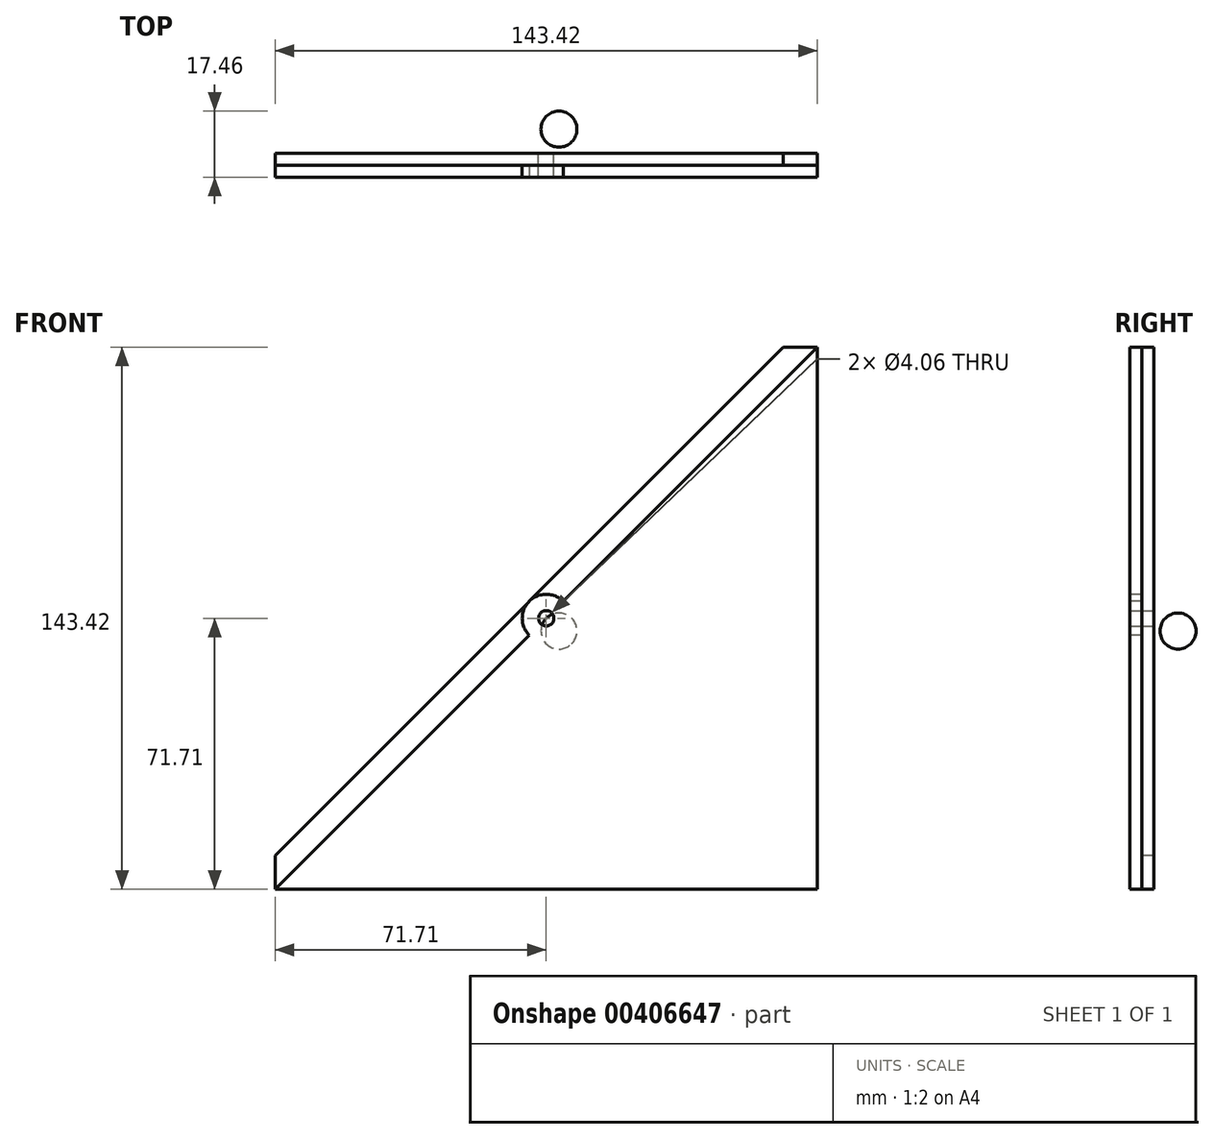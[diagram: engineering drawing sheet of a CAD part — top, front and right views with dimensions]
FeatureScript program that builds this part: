
annotation { "Feature Type Name" : "Feature", "Feature Type Description" : "" }
export const myFeature = defineFeature(function(context is Context, id is Id, definition is map)
    precondition{}
    {
        {
            var Q0;
            Q0=qCreatedBy(makeId("Front.planeOp"),FACE);
            var sketch = newSketch(context, id + "F0", { "sketchPlane" : qUnion([Q0])});
            skLineSegment(sketch, "E0.bottom", {"start": v(-76.2, 76.2) * mm, "end": v(76.2, 76.2) * mm, "construction": true});
            skLineSegment(sketch, "E0.top", {"start": v(-76.2, -76.2) * mm, "end": v(76.2, -76.2) * mm});
            skLineSegment(sketch, "E0.left", {"start": v(-76.2, 76.2) * mm, "end": v(-76.2, -76.2) * mm, "construction": true});
            skLineSegment(sketch, "E0.right", {"start": v(76.2, 76.2) * mm, "end": v(76.2, -76.2) * mm});
            skPoint(sketch, "E0.middle", {"position": v(0, 0) * mm});
            skLineSegment(sketch, "E1", {"start": v(-76.2, -76.2) * mm, "end": v(76.2, 76.2) * mm});
            skLineSegment(sketch, "E2", {"start": v(-76.2, 76.2) * mm, "end": v(76.2, -76.2) * mm, "construction": true});
            skCircle(sketch, "E3", {"center": v(4.5, -4.5) * mm, "radius": 6.35 * mm, "construction": true});
            skCircle(sketch, "E4", {"center": v(4.5, -4.5) * mm, "radius": 2.03 * mm});
            skSolve(sketch);
        }
        {
            var Q0;
            Q0=qSketchRegion(id+"F0",true);
            var Q1;
            Q1=sQuery(id+"F0.wireOp",EDGE,"E0.bottom");
            var Q2;
            Q2=sQuery(id+"F0.wireOp",EDGE,"E0.left");
            extrude(context, id + "F1", {"entities" : qUnion([Q0]), "surfaceEntities" : qUnion([Q1, Q2]), "depth" : 3.17 * mm});
        }
        {
            var Q0;
            Q0=sQuery(id+"F0.wireOp",VERTEX,"E4.center");
            var Q1;
            Q1=qCreatedBy(makeId("Top.planeOp"),FACE);
            cPlane(context, id + "F2", {"entities" : qUnion([Q0, Q1]), "cplaneType" : CPlaneType.PLANE_POINT, "offset" : 25.4 * mm, "width" : 152.4 * mm, "height" : 152.4 * mm});
        }
        {
            var Q0;
            Q0=qCreatedBy(id+"F2.planeOp",FACE);
            var sketch = newSketch(context, id + "F3", { "sketchPlane" : qUnion([Q0])});
            skPoint(sketch, "E5.0", {"position": v(4.5, 0) * mm});
            skLineSegment(sketch, "E6", {"start": v(4.5, 0) * mm, "end": v(4.5, -119.12) * mm});
            skSolve(sketch);
        }
        {
            var Q0;
            Q0=makeQuery(id+"F1.opExtrude","SWEPT_BODY",BODY,{"disambiguationData":[OSD([sQuery(id+"F0.wireOp",EDGE,"E0.top"),sQuery(id+"F0.wireOp",EDGE,"E0.right"),sQuery(id+"F0.wireOp",EDGE,"E1"),sQuery(id+"F0.wireOp",EDGE,"E4")])]});
            var Q1;
            Q1=sQuery(id+"F3.wireOp",EDGE,"E6");
            var Q2;
            Q2=sQuery(id+"F3.wireOp",EDGE,"E6");
            transform(context, id + "F4", {"entities" : qUnion([Q0]), "transformType" : TransformType.ROTATION, "transformAxis" : qUnion([Q2]), "angle" : 90 * degree, "makeCopy" : true});
        }
        {
            var Q0;
            Q0=makeQuery(id+"F4.opPattern","COPY",BODY,{"derivedFrom":makeQuery(id+"F1.opExtrude","SWEPT_BODY",BODY,{"disambiguationData":[OSD([sQuery(id+"F0.wireOp",EDGE,"E0.top"),sQuery(id+"F0.wireOp",EDGE,"E0.right"),sQuery(id+"F0.wireOp",EDGE,"E1"),sQuery(id+"F0.wireOp",EDGE,"E4")])]}),"instanceName":"1"});
            var Q1;
            Q1=sQuery(id+"F3.wireOp",EDGE,"E6");
            transform(context, id + "F5", {"entities" : qUnion([Q0]), "transformType" : TransformType.TRANSLATION_DISTANCE, "transformDirection" : qUnion([Q1]), "distance" : 3.17 * mm, "makeCopy" : false});
        }
        {
            var Q0;
            Q0=makeQuery(id+"F4.opPattern","COPY",FACE,{"derivedFrom":makeQuery(id+"F1.opExtrude","CAP_FACE",FACE,{"disambiguationData":[OSD([sQuery(id+"F0.wireOp",EDGE,"E0.top"),sQuery(id+"F0.wireOp",EDGE,"E0.right"),sQuery(id+"F0.wireOp",EDGE,"E1"),sQuery(id+"F0.wireOp",EDGE,"E4")])],"isStart":false}),"instanceName":"1"});
            var sketch = newSketch(context, id + "F6", { "sketchPlane" : qUnion([Q0])});
            skCircle(sketch, "E7.1", {"center": v(4.5, -4.5) * mm, "radius": 6.35 * mm});
            skSolve(sketch);
        }
        {
            var Q0;
            Q0=qSketchRegion(id+"F6",true);
            extrude(context, id + "F7", {"entities" : qUnion([Q0]), "depth" : 6.35 * mm});
        }
        {
            var Q0;
            Q0=makeQuery(id+"F4.opPattern","COPY",FACE,{"derivedFrom":makeQuery(id+"F1.opExtrude","CAP_FACE",FACE,{"disambiguationData":[OSD([sQuery(id+"F0.wireOp",EDGE,"E0.top"),sQuery(id+"F0.wireOp",EDGE,"E0.right"),sQuery(id+"F0.wireOp",EDGE,"E1"),sQuery(id+"F0.wireOp",EDGE,"E4")])],"isStart":false}),"instanceName":"1"});
            var sketch = newSketch(context, id + "F8", { "sketchPlane" : qUnion([Q0])});
            skArc(sketch, "E8.0", {"start": v(0, 0) * mm, "mid": v(0, -8.98) * mm, "end": v(8.98, -8.98) * mm});
            skLineSegment(sketch, "E9.0", {"start": v(76.2, -85.18) * mm, "end": v(-76.2, 67.22) * mm});
            skLineSegment(sketch, "E10", {"start": v(0, 0) * mm, "end": v(-67.22, 67.22) * mm});
            skLineSegment(sketch, "E11", {"start": v(8.98, -8.98) * mm, "end": v(76.2, -76.2) * mm});
            skLineSegment(sketch, "E12", {"start": v(-76.2, 67.22) * mm, "end": v(-67.22, 67.22) * mm});
            skLineSegment(sketch, "E13", {"start": v(76.2, -85.18) * mm, "end": v(76.2, -76.2) * mm});
            skSolve(sketch);
        }
        {
            var Q0;
            Q0 = qSketchRegion(id + "F8", true);
            extrude(context, id + "F9", {"entities" : qUnion([Q0]), "operationType" : NewBodyOperationType.REMOVE, "endBound" : BoundingType.UP_TO_NEXT, "oppositeDirection" : true, "depth" : 25.4 * mm});
        }
        {
            var Q0;
            Q0=makeQuery(id+"F4.opPattern","COPY",FACE,{"derivedFrom":makeQuery(id+"F1.opExtrude","CAP_FACE",FACE,{"disambiguationData":[OSD([sQuery(id+"F0.wireOp",EDGE,"E0.top"),sQuery(id+"F0.wireOp",EDGE,"E0.right"),sQuery(id+"F0.wireOp",EDGE,"E1"),sQuery(id+"F0.wireOp",EDGE,"E4")])],"isStart":false}),"instanceName":"1"});
            var sketch = newSketch(context, id + "F10", { "sketchPlane" : qUnion([Q0])});
            skPoint(sketch, "E14.0", {"position": v(4.5, -4.5) * mm});
            skLineSegment(sketch, "E15.0", {"start": v(-67.22, 67.22) * mm, "end": v(76.2, 67.22) * mm, "construction": true});
            skLineSegment(sketch, "E15.1", {"start": v(-67.22, 67.22) * mm, "end": v(0, 0) * mm, "construction": true});
            skLineSegment(sketch, "E16", {"start": v(4.5, -4.5) * mm, "end": v(76.2, 67.22) * mm});
            skSolve(sketch);
        }
        {
            var Q0;
            Q0=makeQuery(id+"F1.opExtrude","CAP_FACE",FACE,{"disambiguationData":[OSD([sQuery(id+"F0.wireOp",EDGE,"E0.top"),sQuery(id+"F0.wireOp",EDGE,"E0.right"),sQuery(id+"F0.wireOp",EDGE,"E1"),sQuery(id+"F0.wireOp",EDGE,"E4")])],"isStart":false});
            var sketch = newSketch(context, id + "F11", { "sketchPlane" : qUnion([Q0])});
            skLineSegment(sketch, "E17.0", {"start": v(-76.2, -76.2) * mm, "end": v(76.2, 76.2) * mm, "construction": true});
            skPoint(sketch, "E17.1", {"position": v(4.5, -4.5) * mm});
            skLineSegment(sketch, "E17.2", {"start": v(-76.2, -76.2) * mm, "end": v(76.2, -76.2) * mm, "construction": true});
            skLineSegment(sketch, "E18", {"start": v(76.2, 67.22) * mm, "end": v(-67.22, -76.2) * mm});
            skLineSegment(sketch, "E19.0", {"start": v(76.2, 76.2) * mm, "end": v(76.2, -76.2) * mm, "construction": true});
            skLineSegment(sketch, "E20", {"start": v(4.5, -4.5) * mm, "end": v(76.2, -76.2) * mm});
            skSolve(sketch);
        }
        {
            var Q0;
            {var subQ0=sQuery(id+"F11.wireOp",EDGE,"E18");var subQ1=makeQuery(id+"F1.opExtrude","CAP_EDGE",EDGE,{"disambiguationData":[OSD([sQuery(id+"F0.wireOp",EDGE,"E0.top")])],"isStart":false});var subQ2=makeQuery(id+"F11.imprint","INTERSECT",VERTEX,{"derivedFrom":[subQ1,subQ0]});Q0=makeQuery(id+"F11.imprint","IMPRINT",FACE,{"disambiguationData":[TD([[makeQuery(id+"F11.imprint","IMPRINT",EDGE,{"disambiguationData":[TD([[subQ2,1.0]])],"derivedFrom":subQ0}),1.0]])]});}
            var sketch = newSketch(context, id + "F12", { "sketchPlane" : qUnion([Q0])});
            skLineSegment(sketch, "E21.0", {"start": v(76.2, 67.22) * mm, "end": v(-67.22, -76.2) * mm});
            skLineSegment(sketch, "E22", {"start": v(4.5, -4.5) * mm, "end": v(-14.72, -76.2) * mm});
            skLineSegment(sketch, "E23", {"start": v(4.5, -4.5) * mm, "end": v(23.7, -76.2) * mm});
            skLineSegment(sketch, "E24.0", {"start": v(4.5, -4.5) * mm, "end": v(76.2, -76.2) * mm, "construction": true});
            skLineSegment(sketch, "E25.MirrorCS", {"start": v(4.5, -4.5) * mm, "end": v(76.2, -23.7) * mm});
            skLineSegment(sketch, "E26.MirrorCS", {"start": v(4.5, -4.5) * mm, "end": v(76.2, 14.72) * mm});
            skLineSegment(sketch, "E27.0", {"start": v(-76.2, -76.2) * mm, "end": v(76.2, -76.2) * mm, "construction": true});
            skLineSegment(sketch, "E28", {"start": v(4.5, -4.5) * mm, "end": v(4.5, -76.2) * mm});
            skLineSegment(sketch, "E29.0", {"start": v(76.2, 76.2) * mm, "end": v(76.2, -76.2) * mm, "construction": true});
            skLineSegment(sketch, "E30", {"start": v(4.5, -4.5) * mm, "end": v(76.2, -4.5) * mm});
            skSolve(sketch);
        }
        {
            var Q0;
            Q0=makeQuery(id+"F4.opPattern","COPY",BODY,{"derivedFrom":makeQuery(id+"F1.opExtrude","SWEPT_BODY",BODY,{"disambiguationData":[OSD([sQuery(id+"F0.wireOp",EDGE,"E0.top"),sQuery(id+"F0.wireOp",EDGE,"E0.right"),sQuery(id+"F0.wireOp",EDGE,"E1"),sQuery(id+"F0.wireOp",EDGE,"E4")])]}),"instanceName":"1"});
            var Q1;
            Q1=sQuery(id+"F3.wireOp",EDGE,"E6");
            transform(context, id + "F13", {"entities" : qUnion([Q0]), "transformType" : TransformType.ROTATION, "transformAxis" : qUnion([Q1]), "angle" : 180 * degree, "makeCopy" : false});
        }
        {
            var Q0;
            Q0=makeQuery(id+"F4.opPattern","COPY",FACE,{"derivedFrom":makeQuery(id+"F1.opExtrude","CAP_FACE",FACE,{"disambiguationData":[OSD([sQuery(id+"F0.wireOp",EDGE,"E0.top"),sQuery(id+"F0.wireOp",EDGE,"E0.right"),sQuery(id+"F0.wireOp",EDGE,"E1"),sQuery(id+"F0.wireOp",EDGE,"E4")])],"isStart":false}),"instanceName":"1"});
            var sketch = newSketch(context, id + "F14", { "sketchPlane" : qUnion([Q0])});
            skLineSegment(sketch, "E31.0", {"start": v(76.2, 67.22) * mm, "end": v(-67.22, -76.2) * mm, "construction": true});
            skLineSegment(sketch, "E32.0", {"start": v(76.2, 58.24) * mm, "end": v(-58.24, -76.2) * mm, "construction": true});
            skLineSegment(sketch, "E33", {"start": v(4.5, -4.5) * mm, "end": v(8.98, -8.98) * mm});
            skLineSegment(sketch, "E34.1.0.0", {"start": v(22.45, 13.47) * mm, "end": v(26.94, 8.98) * mm});
            skLineSegment(sketch, "E34.2.0.0", {"start": v(40.41, 31.43) * mm, "end": v(43.78, 28.06) * mm});
            skLineSegment(sketch, "E34.direction1", {"start": v(8.98, -8.98) * mm, "end": v(26.94, 8.98) * mm, "construction": true});
            skLineSegment(sketch, "E34.direction2", {"start": v(8.98, -8.98) * mm, "end": v(-16.37, 16.37) * mm, "construction": true});
            skLineSegment(sketch, "E35.0.3.0", {"start": v(58.37, 49.4) * mm, "end": v(62.86, 44.9) * mm});
            skLineSegment(sketch, "E36.0", {"start": v(79.57, 63.85) * mm, "end": v(-63.85, -79.57) * mm, "construction": true});
            skLineSegment(sketch, "E37.1.0.0", {"start": v(13.48, 4.48) * mm, "end": v(16.84, 1.12) * mm});
            skLineSegment(sketch, "E37.2.0.0", {"start": v(22.48, 13.44) * mm, "end": v(26.97, 8.95) * mm});
            skLineSegment(sketch, "E37.3.0.0", {"start": v(31.47, 22.4) * mm, "end": v(34.8, 19.08) * mm});
            skLineSegment(sketch, "E37.4.0.0", {"start": v(40.47, 31.37) * mm, "end": v(44.96, 26.88) * mm});
            skLineSegment(sketch, "E37.5.0.0", {"start": v(49.46, 40.34) * mm, "end": v(52.76, 37.04) * mm});
            skLineSegment(sketch, "E37.direction1", {"start": v(8.98, -8.98) * mm, "end": v(17.97, -0.01) * mm, "construction": true});
            skLineSegment(sketch, "E38.trimOffspring", {"start": v(17.96, 0) * mm, "end": v(17.97, -0.01) * mm});
            skLineSegment(sketch, "E39.trimOffspring", {"start": v(35.92, 17.96) * mm, "end": v(35.96, 17.92) * mm});
            skPoint(sketch, "E40.orphan", {"position": v(44.9, 26.94) * mm});
            skLineSegment(sketch, "E41.trimOffspring", {"start": v(53.88, 35.92) * mm, "end": v(53.95, 35.85) * mm});
            skLineSegment(sketch, "E42.0", {"start": v(78.45, 64.97) * mm, "end": v(-64.97, -78.45) * mm, "construction": true});
            skLineSegment(sketch, "E43", {"start": v(6.74, -6.74) * mm, "end": v(8.98, -8.98) * mm});
            skLineSegment(sketch, "E44.MirrorCS", {"start": v(24.7, 11.23) * mm, "end": v(26.94, 8.98) * mm});
            skLineSegment(sketch, "E45.MirrorCS", {"start": v(42.66, 29.19) * mm, "end": v(44.9, 26.94) * mm});
            skLineSegment(sketch, "E46.MirrorCS", {"start": v(60.62, 47.15) * mm, "end": v(62.86, 44.9) * mm});
            skSolve(sketch);
        }
        {
            var Q0;
            Q0=makeQuery(id+"F1.opExtrude","CAP_FACE",FACE,{"disambiguationData":[OSD([sQuery(id+"F0.wireOp",EDGE,"E0.top"),sQuery(id+"F0.wireOp",EDGE,"E0.right"),sQuery(id+"F0.wireOp",EDGE,"E1"),sQuery(id+"F0.wireOp",EDGE,"E4")])],"isStart":false});
            var sketch = newSketch(context, id + "F15", { "sketchPlane" : qUnion([Q0])});
            skLineSegment(sketch, "E47.0", {"start": v(76.2, 76.2) * mm, "end": v(76.2, -76.2) * mm, "construction": true});
            skLineSegment(sketch, "E47.1", {"start": v(-76.2, -76.2) * mm, "end": v(76.2, 76.2) * mm, "construction": true});
            skLineSegment(sketch, "E47.2", {"start": v(-76.2, -76.2) * mm, "end": v(76.2, -76.2) * mm, "construction": true});
            skLineSegment(sketch, "E48.0", {"start": v(-67.22, 67.22) * mm, "end": v(-67.22, -76.2) * mm, "construction": true});
            skLineSegment(sketch, "E49", {"start": v(-67.22, -76.2) * mm, "end": v(-67.22, -67.22) * mm});
            skLineSegment(sketch, "E50", {"start": v(-67.22, -67.22) * mm, "end": v(-76.2, -76.2) * mm});
            skLineSegment(sketch, "E51", {"start": v(-67.22, -76.2) * mm, "end": v(-76.2, -76.2) * mm});
            skLineSegment(sketch, "E52.0", {"start": v(8.98, -8.98) * mm, "end": v(76.2, -76.2) * mm, "construction": true});
            skLineSegment(sketch, "E53.MirrorCS", {"start": v(76.2, 67.22) * mm, "end": v(76.2, 76.2) * mm});
            skLineSegment(sketch, "E54.MirrorCS", {"start": v(67.22, 67.22) * mm, "end": v(76.2, 76.2) * mm});
            skLineSegment(sketch, "E55.MirrorCS", {"start": v(76.2, 67.22) * mm, "end": v(67.22, 67.22) * mm});
            skSolve(sketch);
        }
        {
            var Q0;
            Q0 = qSketchRegion(id + "F15", true);
            extrude(context, id + "F16", {"entities" : qUnion([Q0]), "operationType" : NewBodyOperationType.REMOVE, "endBound" : BoundingType.THROUGH_ALL, "oppositeDirection" : true, "depth" : 25.4 * mm});
        }
        {
            var Q0;
            Q0=makeQuery(id+"F7.opExtrude","SWEPT_BODY",BODY,{"disambiguationData":[OSD([sQuery(id+"F6.wireOp",EDGE,"E7.1")])]});
            deleteBodies(context, id + "F17", {"entities" : qUnion([Q0])});
        }
        {
            var Q0;
            Q0=makeQuery(id+"F9.boolean.opBoolean","COPY",FACE,{"derivedFrom":makeQuery(id+"F9.opExtrude","SWEPT_FACE",FACE,{"disambiguationData":[OSD([sQuery(id+"F8.wireOp",EDGE,"E11")])]})});
            var sketch = newSketch(context, id + "F18", { "sketchPlane" : qUnion([Q0])});
            skLineSegment(sketch, "E56.0", {"start": v(12.7, -6.35) * mm, "end": v(0, -6.35) * mm, "construction": true});
            skLineSegment(sketch, "E56.1", {"start": v(6.35, -6.35) * mm, "end": v(6.35, -3.18) * mm, "construction": true});
            skArc(sketch, "E57", {"start": v(6.35, -15.88) * mm, "mid": v(11.11, -11.11) * mm, "end": v(6.35, -6.35) * mm});
            skLineSegment(sketch, "E58", {"start": v(6.35, -6.35) * mm, "end": v(6.35, -15.88) * mm});
            skLineSegment(sketch, "E59", {"start": v(6.35, -15.88) * mm, "end": v(6.35, -20.1) * mm, "construction": true});
            skSolve(sketch);
        }
        {
            var Q0;
            Q0 = qSketchRegion(id + "F18", true);
            var Q1;
            Q1=sQuery(id+"F18.wireOp",EDGE,"E59");
            revolve(context, id + "F19", {"entities" : qUnion([Q0]), "axis" : qUnion([Q1]), "revolveType" : RevolveType.FULL});
        }
        {
            var Q0;
            Q0=makeQuery(id+"F4.opPattern","COPY",BODY,{"derivedFrom":makeQuery(id+"F1.opExtrude","SWEPT_BODY",BODY,{"disambiguationData":[OSD([sQuery(id+"F0.wireOp",EDGE,"E0.top"),sQuery(id+"F0.wireOp",EDGE,"E0.right"),sQuery(id+"F0.wireOp",EDGE,"E1"),sQuery(id+"F0.wireOp",EDGE,"E4")])]}),"instanceName":"1"});
            var Q1;
            Q1=sQuery(id+"F3.wireOp",EDGE,"E6");
            var Q2;
            Q2=sQuery(id+"F3.wireOp",EDGE,"E6");
            transform(context, id + "F20", {"entities" : qUnion([Q0]), "transformType" : TransformType.ROTATION, "transformAxis" : qUnion([Q2]), "angle" : 90 * degree, "makeCopy" : false});
        }
    });
